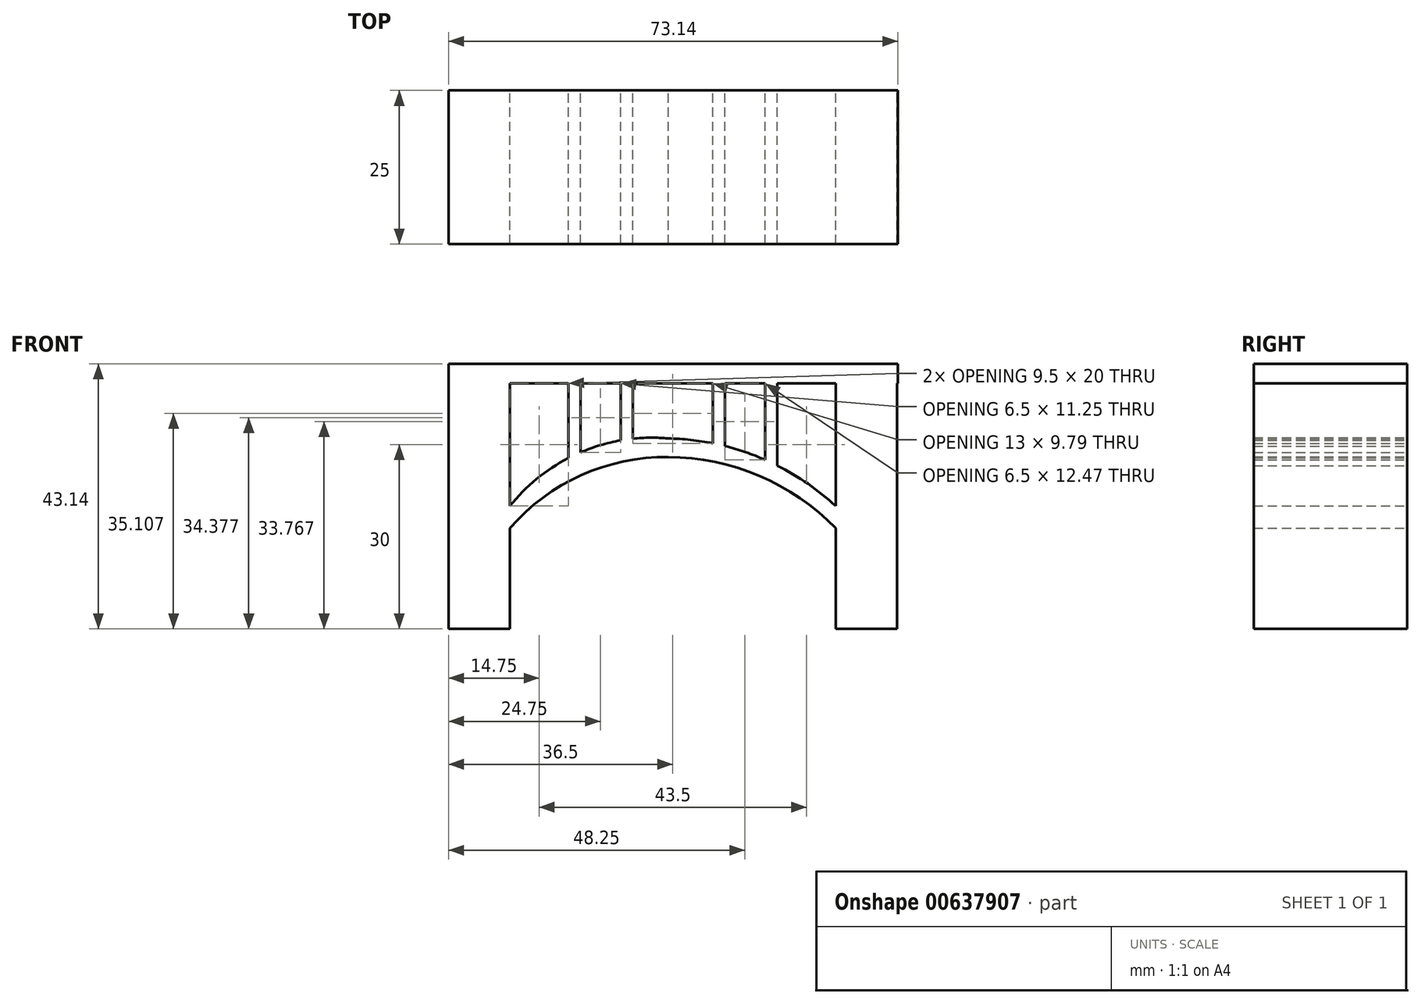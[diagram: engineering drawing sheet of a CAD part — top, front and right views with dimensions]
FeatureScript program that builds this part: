
annotation { "Feature Type Name" : "Feature", "Feature Type Description" : "" }
export const myFeature = defineFeature(function(context is Context, id is Id, definition is map)
    precondition{}
    {
        {
            var Q0;
            Q0=qCreatedBy(makeId("Front.planeOp"),FACE);
            var sketch = newSketch(context, id + "F0", { "sketchPlane" : qUnion([Q0])});
            skLineSegment(sketch, "E0.bottom", {"start": v(0, 0) * mm, "end": v(10, 0) * mm});
            skLineSegment(sketch, "E0.top", {"start": v(0, 40) * mm, "end": v(10, 40) * mm});
            skLineSegment(sketch, "E0.left", {"start": v(0, 0) * mm, "end": v(0, 40) * mm});
            skLineSegment(sketch, "E0.right", {"start": v(10, 0) * mm, "end": v(10, 40) * mm});
            skLineSegment(sketch, "E1.bottom", {"start": v(73, 0) * mm, "end": v(63, 0) * mm});
            skLineSegment(sketch, "E1.top", {"start": v(73, 40) * mm, "end": v(63, 40) * mm});
            skLineSegment(sketch, "E1.left", {"start": v(73, 0) * mm, "end": v(73, 40) * mm});
            skLineSegment(sketch, "E1.right", {"start": v(63, 0) * mm, "end": v(63, 40) * mm});
            skArc(sketch, "E2", {"start": v(35.78, 31.01) * mm, "mid": v(21.5, 28.75) * mm, "end": v(10, 20) * mm});
            skArc(sketch, "E3", {"start": v(63, 20) * mm, "mid": v(50.4, 28) * mm, "end": v(35.78, 31.01) * mm});
            skArc(sketch, "E4", {"start": v(35.78, 28) * mm, "mid": v(21.62, 25.03) * mm, "end": v(10, 16.41) * mm});
            skPoint(sketch, "E4.startSnap0", {"position": v(50.4, 28) * mm});
            skArc(sketch, "E5", {"start": v(63, 16.41) * mm, "mid": v(50.54, 24.92) * mm, "end": v(35.78, 28) * mm});
            skLineSegment(sketch, "E6.bottom", {"start": v(0, 40) * mm, "end": v(73.14, 40) * mm});
            skLineSegment(sketch, "E6.top", {"start": v(0, 43.14) * mm, "end": v(73.14, 43.14) * mm});
            skLineSegment(sketch, "E6.left", {"start": v(0, 40) * mm, "end": v(0, 43.14) * mm});
            skLineSegment(sketch, "E6.right", {"start": v(73.14, 40) * mm, "end": v(73.14, 43.14) * mm});
            skLineSegment(sketch, "E7", {"start": v(19.5, 40) * mm, "end": v(19.5, 27.8) * mm});
            skLineSegment(sketch, "E8", {"start": v(21.5, 28.75) * mm, "end": v(21.5, 40) * mm});
            skLineSegment(sketch, "E9", {"start": v(53.5, 40) * mm, "end": v(53.5, 26.6) * mm});
            skLineSegment(sketch, "E10", {"start": v(51.5, 40) * mm, "end": v(51.5, 28) * mm});
            skLineSegment(sketch, "E11", {"start": v(45, 40) * mm, "end": v(45, 29.76) * mm});
            skLineSegment(sketch, "E12", {"start": v(43, 40) * mm, "end": v(43, 30.21) * mm});
            skLineSegment(sketch, "E13", {"start": v(28, 40) * mm, "end": v(28, 30.68) * mm});
            skLineSegment(sketch, "E14", {"start": v(30, 40) * mm, "end": v(30, 30.97) * mm});
            skLineSegment(sketch, "E15", {"start": v(35.5, 40) * mm, "end": v(35.5, 31.03) * mm});
            skLineSegment(sketch, "E16", {"start": v(37.5, 40) * mm, "end": v(37.5, 31.01) * mm});
            skLineSegment(sketch, "E17.bottom", {"start": v(35.5, 40) * mm, "end": v(37.5, 40) * mm});
            skLineSegment(sketch, "E17.right", {"start": v(37.5, 40) * mm, "end": v(37.5, 30.91) * mm});
            skLineSegment(sketch, "E18", {"start": v(37.5, 31.01) * mm, "end": v(37.5, 30.91) * mm});
            skPoint(sketch, "E19.orphan", {"position": v(37.5, 30.42) * mm});
            skLineSegment(sketch, "E20", {"start": v(35.5, 31.03) * mm, "end": v(35.5, 31.02) * mm});
            skPoint(sketch, "E21.orphan", {"position": v(35.5, 31.02) * mm});
            skPoint(sketch, "E22.start.orphan", {"position": v(35.5, 31.01) * mm});
            skLineSegment(sketch, "E23.left", {"start": v(51.5, 28) * mm, "end": v(51.5, 27.5) * mm});
            skLineSegment(sketch, "E23.right", {"start": v(53.5, 28) * mm, "end": v(53.5, 26.56) * mm});
            skLineSegment(sketch, "E24", {"start": v(53.5, 26.6) * mm, "end": v(53.5, 26.56) * mm});
            skPoint(sketch, "E23.top.end.orphan", {"position": v(53.5, 26.21) * mm});
            skSolve(sketch);
        }
        {
            var Q0;
            Q0 = qSketchRegion(id + "F0", true);
            var Q1;
            {var subQ0=sQuery(id+"F0.wireOp",EDGE,"E7");Q1=makeQuery(id+"F0.imprint","IMPRINT",FACE,{"disambiguationData":[TD([[makeQuery(id+"F0.imprint","IMPRINT",EDGE,{"derivedFrom":subQ0}),1.0]])]});}
            var Q2;
            {var subQ0=sQuery(id+"F0.wireOp",EDGE,"E13");Q2=makeQuery(id+"F0.imprint","IMPRINT",FACE,{"disambiguationData":[TD([[makeQuery(id+"F0.imprint","IMPRINT",EDGE,{"derivedFrom":subQ0}),1.0]])]});}
            var Q3;
            Q3=makeQuery(id+"F0.imprint","IMPRINT",FACE,{"disambiguationData":[TD([[makeQuery(id+"F0.imprint","IMPRINT",EDGE,{"derivedFrom":sQuery(id+"F0.wireOp",EDGE,"E17.bottom")}),-1.0]])]});
            var Q4;
            {var subQ0=sQuery(id+"F0.wireOp",EDGE,"E11");Q4=makeQuery(id+"F0.imprint","IMPRINT",FACE,{"disambiguationData":[TD([[makeQuery(id+"F0.imprint","IMPRINT",EDGE,{"derivedFrom":subQ0}),-1.0]])]});}
            var Q5;
            {var subQ1=sQuery(id+"F0.wireOp",EDGE,"E9");Q5=makeQuery(id+"F0.imprint","IMPRINT",FACE,{"disambiguationData":[TD([[makeQuery(id+"F0.imprint","IMPRINT",EDGE,{"derivedFrom":subQ1}),-1.0]])]});}
            extrude(context, id + "F1", {"entities" : qUnion([Q0, Q1, Q2, Q3, Q4, Q5]), "depth" : 25 * mm, "offsetDistance" : 25 * mm});
        }
    });
